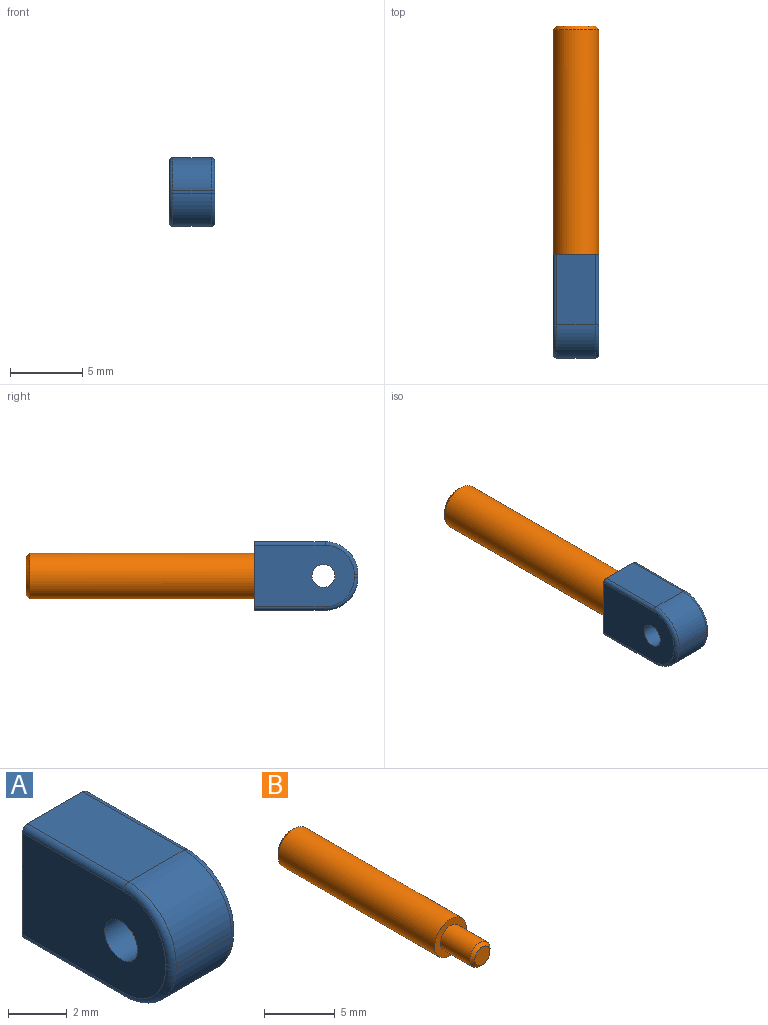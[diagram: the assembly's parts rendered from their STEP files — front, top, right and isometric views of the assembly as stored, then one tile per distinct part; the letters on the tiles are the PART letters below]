
ASSEMBLY  parts=2 mates=1
PART A: 21 faces, bbox 3.2x7.4x5.1 mm
  f0: plane 4.88x2.67mm, normal (0,0,1), area 13mm2, adj f5,f7,f11,f16
  f1: plane 6.91x4.25mm, normal (-1,0,0), area 25.6mm2, adj f5,f10,f16,f17,f18,f19,f20
  f2: plane 4.88x2.67mm, normal (0,0,-1), area 13mm2, adj f5,f6,f15,f20
  f3: plane 6.91x4.25mm, normal (1,0,0), area 25.6mm2, adj f5,f10,f11,f12,f13,f14,f15
  f4: plane 2.67x0.19mm, normal (0,-1,0), area 0.5mm2, adj f6,f7,f13,f18
  f5: plane 4.76x3.18mm, normal (0,1,0), area 10.6mm2, adj f0,f1,f2,f3,f8,f11,f15,f16
  f6: cylinder r=2.29mm len=2.67mm, axis (-1,0,0), area 9.6mm2, adj f2,f4,f14,f19
  f7: cylinder r=2.29mm len=2.67mm, axis (1,0,0), area 9.6mm2, adj f0,f4,f12,f17
  f8: cylinder r=1.19mm len=3.18mm, axis (0,1,0), area 23.8mm2, adj f5,f9
  f9: plane 2.38x2.38mm, normal (0,1,0), area 4.5mm2, adj f8
  f10: cylinder r=0.79mm len=3.18mm, axis (1,0,0), area 15.8mm2, adj f1,f3
  f11: cylinder r=0.25mm len=4.88mm, axis (0,-1,0), area 1.9mm2, adj f0,f3,f5,f12
  f12: torus R=2.03mm, axis (-1,0,0), area 1.4mm2, adj f3,f7,f11,f13
  f13: cylinder r=0.25mm len=0.25mm, axis (0,0,-1), area 0.1mm2, adj f3,f4,f12,f14
  f14: torus R=2.03mm, axis (-1,0,0), area 1.4mm2, adj f3,f6,f13,f15
  f15: cylinder r=0.25mm len=4.88mm, axis (0,1,0), area 1.9mm2, adj f2,f3,f5,f14
  f16: cylinder r=0.25mm len=4.88mm, axis (0,1,0), area 1.9mm2, adj f0,f1,f5,f17
  f17: torus R=2.03mm, axis (-1,0,0), area 1.4mm2, adj f1,f7,f16,f18
  f18: cylinder r=0.25mm len=0.25mm, axis (0,0,1), area 0.1mm2, adj f1,f4,f17,f19
  f19: torus R=2.03mm, axis (-1,0,0), area 1.4mm2, adj f1,f6,f18,f20
  f20: cylinder r=0.25mm len=4.88mm, axis (0,-1,0), area 1.9mm2, adj f1,f2,f5,f19
PART B: 7 faces, bbox 3.2x19.1x3.2 mm
  f0: cylinder r=1.59mm len=15.62mm, axis (0,-1,0), area 155.8mm2, adj f2,f6
  f1: plane 2.67x2.67mm, normal (0,1,0), area 5.6mm2, adj f6
  f2: plane 3.18x3.18mm, normal (0,-1,0), area 4.7mm2, adj f0,f3
  f3: cylinder r=1.02mm len=2.92mm, axis (0,1,0), area 18.6mm2, adj f2,f5
  f4: plane 1.52x1.52mm, normal (0,-1,0), area 1.8mm2, adj f5
  f5: cone r=0.76mm half-angle=45deg, axis (0,1,0), area 2mm2, adj f3,f4
  f6: cone r=1.59mm half-angle=45deg, axis (0,-1,0), area 3.3mm2, adj f0,f1
PLACE A t=(-5.67,2.44,3.19)mm
PLACE B t=(-5.67,2.44,3.19)mm
MATE fastened B.f0 <-> A.f8  axis (0,-1,0) through (-5.67,2.44,3.19)mm
